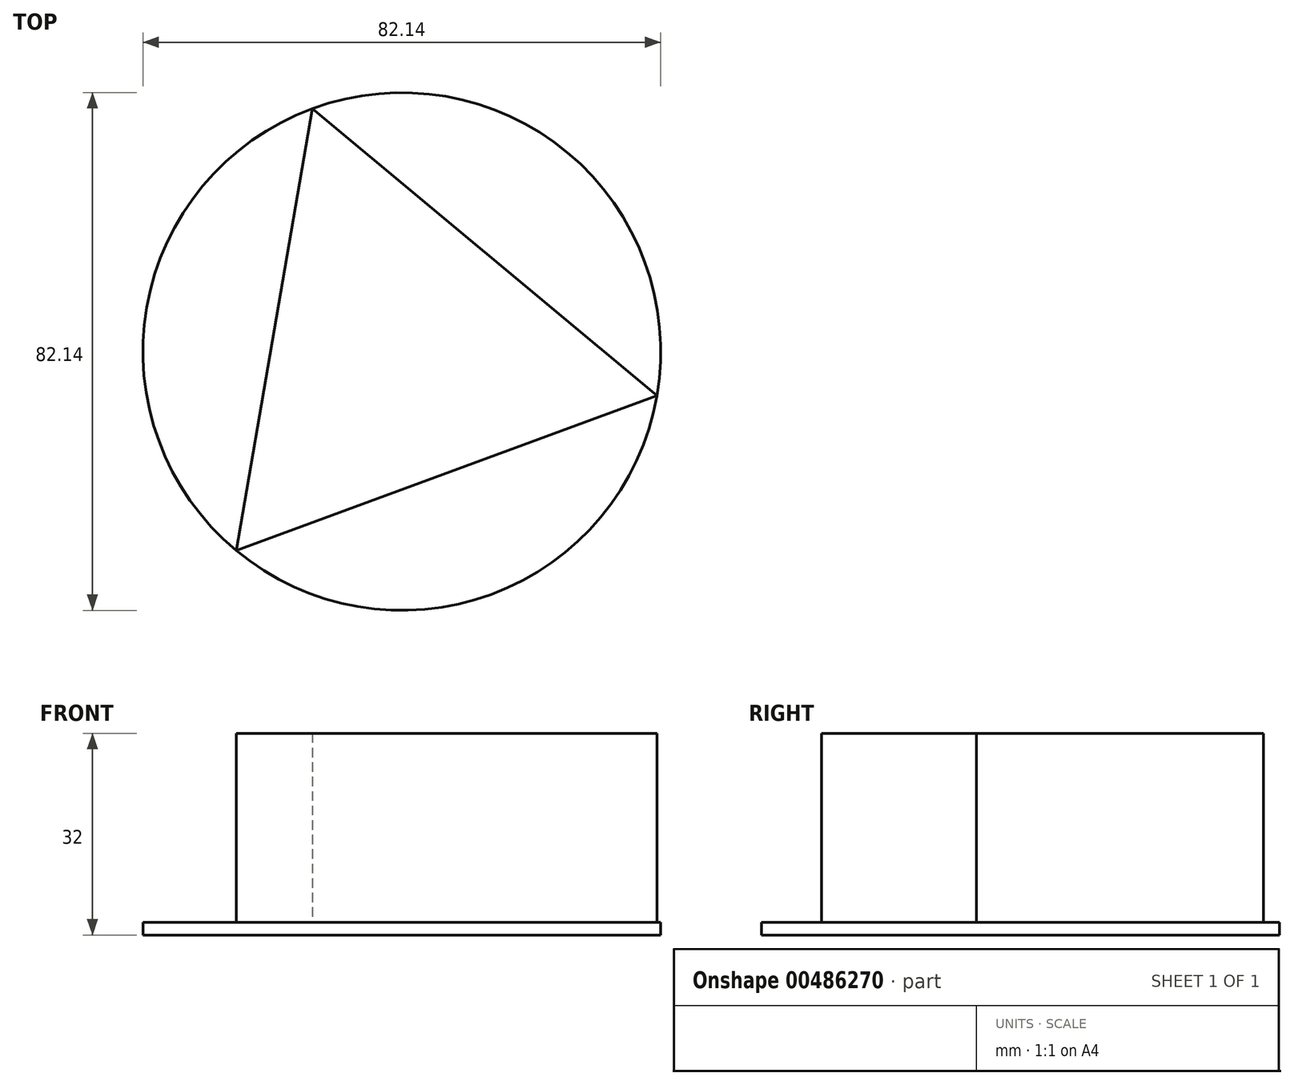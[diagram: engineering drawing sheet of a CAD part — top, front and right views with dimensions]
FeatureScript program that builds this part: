
annotation { "Feature Type Name" : "Feature", "Feature Type Description" : "" }
export const myFeature = defineFeature(function(context is Context, id is Id, definition is map)
    precondition{}
    {
        {
            var Q0;
            Q0=qCreatedBy(makeId("Top.planeOp"),FACE);
            var sketch = newSketch(context, id + "F0", { "sketchPlane" : qUnion([Q0])});
            skCircle(sketch, "E0", {"center": v(0, 0) * mm, "radius": 41.07 * mm});
            skSolve(sketch);
        }
        {
            var Q0;
            Q0 = qSketchRegion(id + "F0", true);
            extrude(context, id + "F1", {"entities" : qUnion([Q0]), "depth" : 2 * mm});
        }
        {
            var Q0;
            Q0=makeQuery(id+"F1.opExtrude","CAP_FACE",FACE,{"disambiguationData":[OSD([sQuery(id+"F0.wireOp",EDGE,"E0")])],"isStart":false});
            var sketch = newSketch(context, id + "F2", { "sketchPlane" : qUnion([Q0])});
            skCircle(sketch, "E1.cCircle", {"center": v(0, 0) * mm, "radius": 41.07 * mm, "construction": true});
            skLineSegment(sketch, "E1.0", {"start": v(-14.2, 38.54) * mm, "end": v(40.47, -6.98) * mm});
            skLineSegment(sketch, "E1.1", {"start": v(40.47, -6.98) * mm, "end": v(-26.28, -31.56) * mm});
            skLineSegment(sketch, "E1.2", {"start": v(-26.28, -31.56) * mm, "end": v(-14.2, 38.54) * mm});
            skSolve(sketch);
        }
        {
            var Q0;
            Q0 = qSketchRegion(id + "F2", true);
            extrude(context, id + "F3", {"entities" : qUnion([Q0]), "operationType" : NewBodyOperationType.ADD, "depth" : 30 * mm});
        }
    });
